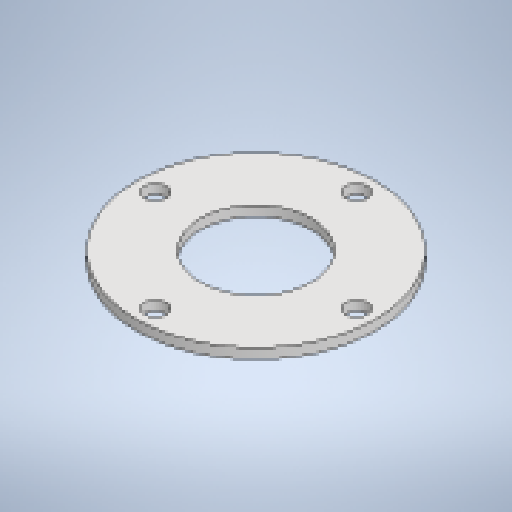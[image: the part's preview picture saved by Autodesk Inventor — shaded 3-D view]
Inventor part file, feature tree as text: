
AUTODESK INVENTOR PART (.ipt)
format: ipt  version: 2025 (Build 290162010, 162A)  size: 197,120 bytes
history: native  units: mm
features: other x3, sketch x2, sheet_metal_op x1, pattern_circular x1
ambient origin geometry x8: Origin, YZ Plane, XZ Plane, XY Plane, X Axis, Y Axis, Z Axis, Center Point
bodies: Body1 (feature_tree)
feature tree (7):
  sheet_metal_op  "Face2"
  pattern_circular  "Circular Pattern1"  [2 undecoded]
  sketch  "Sketch2"  dims[d14=8.0mm]
  other  "Plate2"
  sketch  "Sketch3"  dims[d15=17.0mm d17=8.0mm d18=0.0mm d19=40.0mm d20=360.0deg d25=91.0mm d27=190.0mm d28=160.0mm]
  other  "Cut1"
  other  "Definition1"
note: 2 required parameter values undecoded (feature->parameter linkage not recoverable at this tier; creation-order binding heuristic only, values carry confidence <= 0.55)
